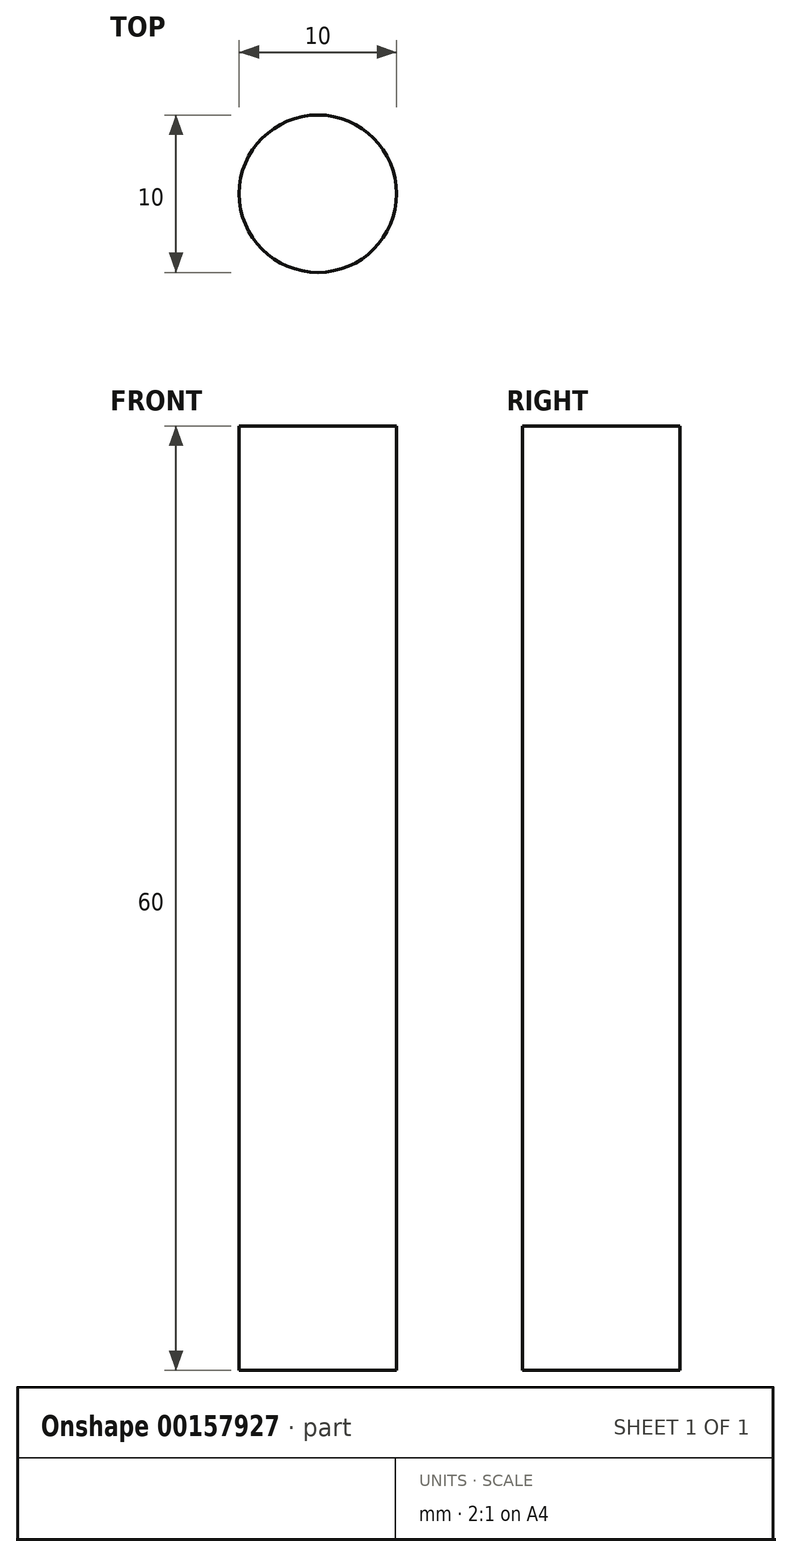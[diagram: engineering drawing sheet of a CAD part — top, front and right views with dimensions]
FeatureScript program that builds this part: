
annotation { "Feature Type Name" : "Feature", "Feature Type Description" : "" }
export const myFeature = defineFeature(function(context is Context, id is Id, definition is map)
    precondition{}
    {
        {
            var Q0;
            Q0=qCreatedBy(makeId("Top.planeOp"),FACE);
            var sketch = newSketch(context, id + "F0", { "sketchPlane" : qUnion([Q0])});
            skCircle(sketch, "E0", {"center": v(0, 0) * mm, "radius": 5 * mm});
            skSolve(sketch);
        }
        {
            var Q0;
            Q0=makeQuery(id+"F0.imprint","IMPRINT",FACE,{"disambiguationData":[TD([[makeQuery(id+"F0.imprint","IMPRINT",EDGE,{"derivedFrom":sQuery(id+"F0.wireOp",EDGE,"E0")}),1.0]])]});
            extrude(context, id + "F1", {"entities" : qUnion([Q0]), "depth" : 60 * mm});
        }
    });
